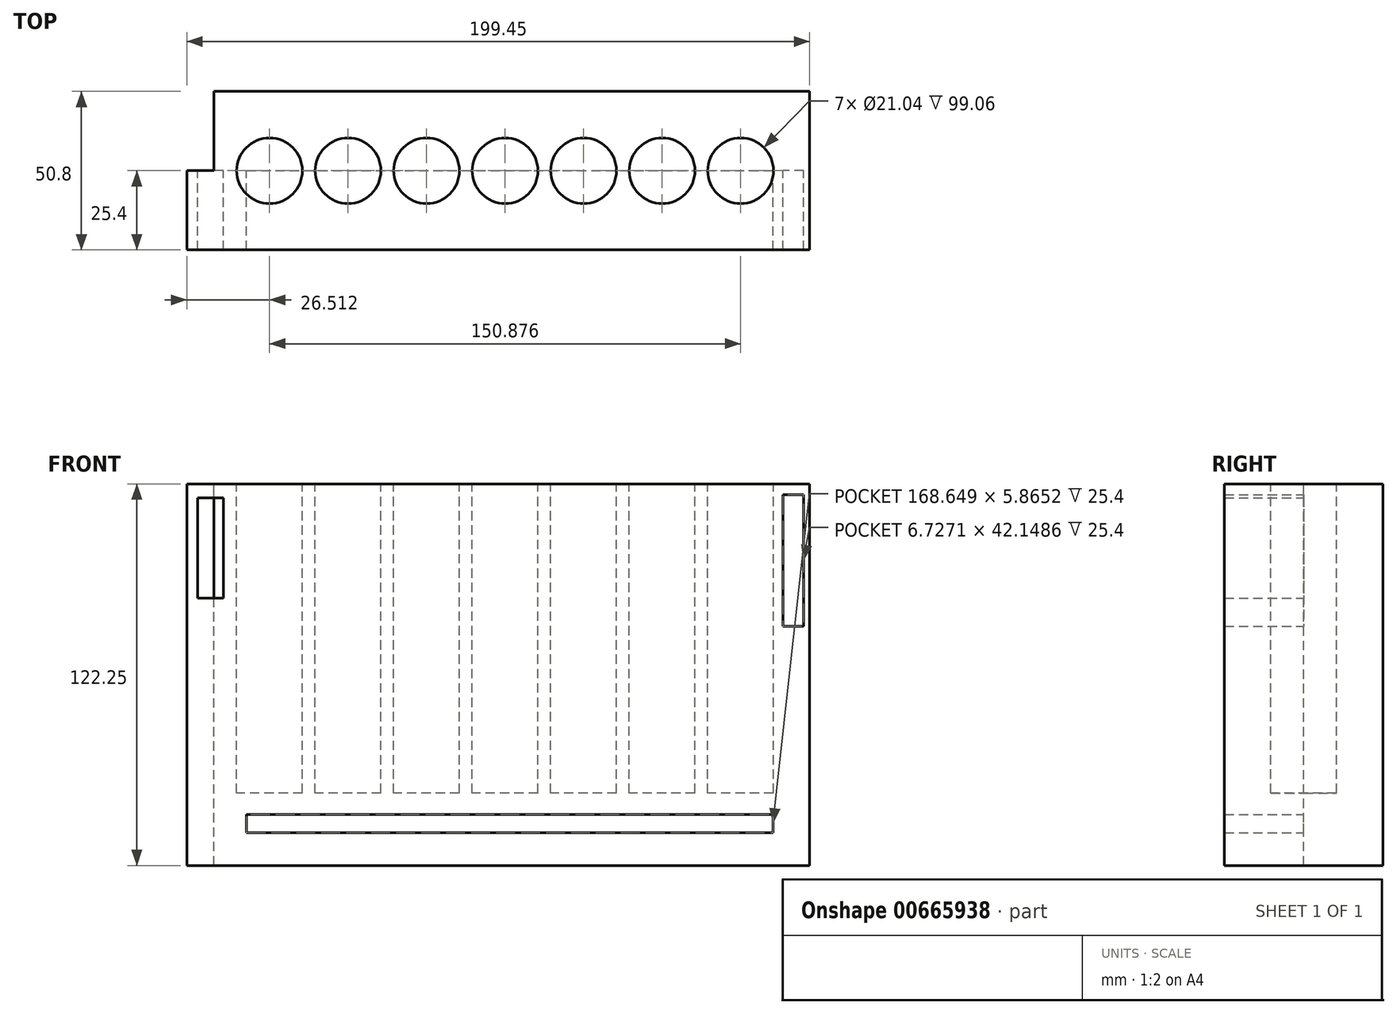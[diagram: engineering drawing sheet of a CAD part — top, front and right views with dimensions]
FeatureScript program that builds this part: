
annotation { "Feature Type Name" : "Feature", "Feature Type Description" : "" }
export const myFeature = defineFeature(function(context is Context, id is Id, definition is map)
    precondition{}
    {
        {
            var Q0;
            Q0=qCreatedBy(makeId("Front.planeOp"),FACE);
            var sketch = newSketch(context, id + "F0", { "sketchPlane" : qUnion([Q0])});
            skLineSegment(sketch, "E0.bottom", {"start": v(-91.64, -10.45) * mm, "end": v(99.17, -10.45) * mm});
            skLineSegment(sketch, "E0.top", {"start": v(-91.64, 111.8) * mm, "end": v(99.17, 111.8) * mm});
            skLineSegment(sketch, "E0.left", {"start": v(-91.64, -10.45) * mm, "end": v(-91.64, 111.8) * mm});
            skLineSegment(sketch, "E0.right", {"start": v(99.17, -10.45) * mm, "end": v(99.17, 111.8) * mm});
            skSolve(sketch);
        }
        {
            var Q0;
            Q0 = qSketchRegion(id + "F0", true);
            extrude(context, id + "F1", {"entities" : qUnion([Q0]), "depth" : 25.4 * mm, "offsetDistance" : 25.4 * mm});
        }
        {
            var Q0;
            Q0=makeQuery(id+"F1.opExtrude","SWEPT_FACE",FACE,{"disambiguationData":[OSD([sQuery(id+"F0.wireOp",EDGE,"E0.top")])]});
            var sketch = newSketch(context, id + "F2", { "sketchPlane" : qUnion([Q0])});
            skCircle(sketch, "E1", {"center": v(-73.77, -25.4) * mm, "radius": 10.52 * mm});
            skCircle(sketch, "E2.1.0.0", {"center": v(-48.62, -25.4) * mm, "radius": 10.52 * mm});
            skCircle(sketch, "E2.2.0.0", {"center": v(-23.48, -25.4) * mm, "radius": 10.52 * mm});
            skCircle(sketch, "E2.3.0.0", {"center": v(1.67, -25.4) * mm, "radius": 10.52 * mm});
            skCircle(sketch, "E2.4.0.0", {"center": v(26.82, -25.4) * mm, "radius": 10.52 * mm});
            skCircle(sketch, "E2.5.0.0", {"center": v(51.96, -25.4) * mm, "radius": 10.52 * mm});
            skCircle(sketch, "E2.6.0.0", {"center": v(77.1, -25.4) * mm, "radius": 10.52 * mm});
            skLineSegment(sketch, "E2.direction1", {"start": v(-73.77, -25.4) * mm, "end": v(-48.62, -25.4) * mm, "construction": true});
            skSolve(sketch);
        }
        {
            var Q0;
            {var subQ0=sQuery(id+"F2.wireOp",EDGE,"E1");var subQ1=makeQuery(id+"F1.opExtrude","CAP_EDGE",EDGE,{"disambiguationData":[OSD([sQuery(id+"F0.wireOp",EDGE,"E0.top")])],"isStart":false});var subQ2=makeQuery(id+"F2.imprint","INTERSECT",VERTEX,{"disambiguationData":[OD(0.0)],"derivedFrom":[subQ1,subQ0]});Q0=makeQuery(id+"F2.imprint","IMPRINT",FACE,{"disambiguationData":[TD([[makeQuery(id+"F2.imprint","IMPRINT",EDGE,{"disambiguationData":[TD([[subQ2,1.0]])],"derivedFrom":subQ0}),1.0]])]});}
            var Q1;
            {var subQ0=sQuery(id+"F2.wireOp",EDGE,"E2.1.0.0");var subQ1=makeQuery(id+"F1.opExtrude","CAP_EDGE",EDGE,{"disambiguationData":[OSD([sQuery(id+"F0.wireOp",EDGE,"E0.top")])],"isStart":false});var subQ2=makeQuery(id+"F2.imprint","INTERSECT",VERTEX,{"disambiguationData":[OD(0.0)],"derivedFrom":[subQ1,subQ0]});Q1=makeQuery(id+"F2.imprint","IMPRINT",FACE,{"disambiguationData":[TD([[makeQuery(id+"F2.imprint","IMPRINT",EDGE,{"disambiguationData":[TD([[subQ2,1.0]])],"derivedFrom":subQ0}),1.0]])]});}
            var Q2;
            {var subQ0=sQuery(id+"F2.wireOp",EDGE,"E2.2.0.0");var subQ1=makeQuery(id+"F1.opExtrude","CAP_EDGE",EDGE,{"disambiguationData":[OSD([sQuery(id+"F0.wireOp",EDGE,"E0.top")])],"isStart":false});var subQ2=makeQuery(id+"F2.imprint","INTERSECT",VERTEX,{"disambiguationData":[OD(0.0)],"derivedFrom":[subQ1,subQ0]});Q2=makeQuery(id+"F2.imprint","IMPRINT",FACE,{"disambiguationData":[TD([[makeQuery(id+"F2.imprint","IMPRINT",EDGE,{"disambiguationData":[TD([[subQ2,1.0]])],"derivedFrom":subQ0}),1.0]])]});}
            var Q3;
            {var subQ0=sQuery(id+"F2.wireOp",EDGE,"E2.3.0.0");var subQ1=makeQuery(id+"F1.opExtrude","CAP_EDGE",EDGE,{"disambiguationData":[OSD([sQuery(id+"F0.wireOp",EDGE,"E0.top")])],"isStart":false});var subQ2=makeQuery(id+"F2.imprint","INTERSECT",VERTEX,{"disambiguationData":[OD(0.0)],"derivedFrom":[subQ1,subQ0]});Q3=makeQuery(id+"F2.imprint","IMPRINT",FACE,{"disambiguationData":[TD([[makeQuery(id+"F2.imprint","IMPRINT",EDGE,{"disambiguationData":[TD([[subQ2,1.0]])],"derivedFrom":subQ0}),1.0]])]});}
            var Q4;
            {var subQ0=sQuery(id+"F2.wireOp",EDGE,"E2.4.0.0");var subQ1=makeQuery(id+"F1.opExtrude","CAP_EDGE",EDGE,{"disambiguationData":[OSD([sQuery(id+"F0.wireOp",EDGE,"E0.top")])],"isStart":false});var subQ2=makeQuery(id+"F2.imprint","INTERSECT",VERTEX,{"disambiguationData":[OD(0.0)],"derivedFrom":[subQ1,subQ0]});Q4=makeQuery(id+"F2.imprint","IMPRINT",FACE,{"disambiguationData":[TD([[makeQuery(id+"F2.imprint","IMPRINT",EDGE,{"disambiguationData":[TD([[subQ2,-1.0]])],"derivedFrom":subQ0}),1.0]])]});}
            var Q5;
            {var subQ0=sQuery(id+"F2.wireOp",EDGE,"E2.6.0.0");var subQ1=makeQuery(id+"F1.opExtrude","CAP_EDGE",EDGE,{"disambiguationData":[OSD([sQuery(id+"F0.wireOp",EDGE,"E0.top")])],"isStart":false});var subQ2=makeQuery(id+"F2.imprint","INTERSECT",VERTEX,{"disambiguationData":[OD(0.0)],"derivedFrom":[subQ1,subQ0]});Q5=makeQuery(id+"F2.imprint","IMPRINT",FACE,{"disambiguationData":[TD([[makeQuery(id+"F2.imprint","IMPRINT",EDGE,{"disambiguationData":[TD([[subQ2,-1.0]])],"derivedFrom":subQ0}),1.0]])]});}
            var Q6;
            {var subQ0=sQuery(id+"F2.wireOp",EDGE,"E2.5.0.0");var subQ1=makeQuery(id+"F1.opExtrude","CAP_EDGE",EDGE,{"disambiguationData":[OSD([sQuery(id+"F0.wireOp",EDGE,"E0.top")])],"isStart":false});var subQ2=makeQuery(id+"F2.imprint","INTERSECT",VERTEX,{"disambiguationData":[OD(0.0)],"derivedFrom":[subQ1,subQ0]});Q6=makeQuery(id+"F2.imprint","IMPRINT",FACE,{"disambiguationData":[TD([[makeQuery(id+"F2.imprint","IMPRINT",EDGE,{"disambiguationData":[TD([[subQ2,-1.0]])],"derivedFrom":subQ0}),1.0]])]});}
            extrude(context, id + "F3", {"entities" : qUnion([Q0, Q1, Q2, Q3, Q4, Q5, Q6]), "operationType" : NewBodyOperationType.REMOVE, "oppositeDirection" : true, "depth" : 99.06 * mm, "offsetDistance" : 25.4 * mm});
        }
        {
            var Q0;
            Q0=makeQuery(id+"F1.opExtrude","CAP_FACE",FACE,{"disambiguationData":[OSD([sQuery(id+"F0.wireOp",EDGE,"E0.bottom"),sQuery(id+"F0.wireOp",EDGE,"E0.top"),sQuery(id+"F0.wireOp",EDGE,"E0.left"),sQuery(id+"F0.wireOp",EDGE,"E0.right")])],"isStart":false});
            var sketch = newSketch(context, id + "F4", { "sketchPlane" : qUnion([Q0])});
            skCircle(sketch, "E3", {"center": v(-73.77, 12.74) * mm, "radius": 23.19 * mm});
            skSolve(sketch);
        }
        {
            var Q0;
            Q0=makeQuery(id+"F1.opExtrude","SWEPT_BODY",BODY,{"disambiguationData":[OSD([sQuery(id+"F0.wireOp",EDGE,"E0.bottom"),sQuery(id+"F0.wireOp",EDGE,"E0.top"),sQuery(id+"F0.wireOp",EDGE,"E0.left"),sQuery(id+"F0.wireOp",EDGE,"E0.right")])]});
            var Q1;
            {var subQ0=sQuery(id+"F0.wireOp",EDGE,"E0.right");var subQ24=makeQuery(id+"F1.opExtrude","CAP_EDGE",EDGE,{"disambiguationData":[OSD([subQ0])],"isStart":false});Q1=makeQuery(id+"F4.imprint","IMPRINT",FACE,{"disambiguationData":[TD([[makeQuery(id+"F4.imprint","IMPRINT",EDGE,{"derivedFrom":subQ24}),1.0]])]});}
            mirror(context, id + "F5", {"entities" : qUnion([Q0]), "mirrorPlane" : qUnion([Q1])});
        }
        {
            var Q0;
            Q0=makeQuery(id+"F5.opPattern","COPY",FACE,{"derivedFrom":makeQuery(id+"F1.opExtrude","CAP_FACE",FACE,{"disambiguationData":[OSD([sQuery(id+"F0.wireOp",EDGE,"E0.bottom"),sQuery(id+"F0.wireOp",EDGE,"E0.top"),sQuery(id+"F0.wireOp",EDGE,"E0.left"),sQuery(id+"F0.wireOp",EDGE,"E0.right")])],"isStart":false}),"instanceName":"1"});
            var sketch = newSketch(context, id + "F6", { "sketchPlane" : qUnion([Q0])});
            skLineSegment(sketch, "E4.bottom", {"start": v(81.13, 0) * mm, "end": v(-87.52, 0) * mm});
            skLineSegment(sketch, "E4.top", {"start": v(81.13, 5.87) * mm, "end": v(-87.52, 5.87) * mm});
            skLineSegment(sketch, "E4.left", {"start": v(81.13, 0) * mm, "end": v(81.13, 5.87) * mm});
            skLineSegment(sketch, "E4.right", {"start": v(-87.52, 0) * mm, "end": v(-87.52, 5.87) * mm});
            skSolve(sketch);
        }
        {
            var Q0;
            Q0 = qSketchRegion(id + "F6", true);
            extrude(context, id + "F7", {"entities" : qUnion([Q0]), "operationType" : NewBodyOperationType.REMOVE, "oppositeDirection" : true, "depth" : 25.4 * mm, "offsetDistance" : 25.4 * mm});
        }
        {
            var Q0;
            Q0=makeQuery(id+"F5.opPattern","COPY",FACE,{"derivedFrom":makeQuery(id+"F1.opExtrude","SWEPT_FACE",FACE,{"disambiguationData":[OSD([sQuery(id+"F0.wireOp",EDGE,"E0.left")])]}),"instanceName":"1"});
            extrude(context, id + "F8", {"entities" : qUnion([Q0]), "operationType" : NewBodyOperationType.ADD, "depth" : 8.64 * mm, "offsetDistance" : 25.4 * mm});
        }
        {
            var Q0;
            {var subQ0=sQuery(id+"F0.wireOp",EDGE,"E0.left");Q0=makeQuery(id+"F8.boolean.opBoolean","MERGE",FACE,{"derivedFrom":[makeQuery(id+"F5.opPattern","COPY",FACE,{"derivedFrom":makeQuery(id+"F1.opExtrude","CAP_FACE",FACE,{"disambiguationData":[OSD([sQuery(id+"F0.wireOp",EDGE,"E0.bottom"),sQuery(id+"F0.wireOp",EDGE,"E0.top"),subQ0,sQuery(id+"F0.wireOp",EDGE,"E0.right")])],"isStart":false}),"instanceName":"1"}),makeQuery(id+"F8.opExtrude","SWEPT_FACE",FACE,{"disambiguationData":[OSD([subQ0]),TDD([makeQuery(id+"F5.opPattern","COPY",EDGE,{"derivedFrom":makeQuery(id+"F1.opExtrude","CAP_EDGE",EDGE,{"disambiguationData":[OSD([subQ0])],"isStart":false}),"instanceName":"1"})])]})]});}
            var sketch = newSketch(context, id + "F9", { "sketchPlane" : qUnion([Q0])});
            skLineSegment(sketch, "E5.bottom", {"start": v(-97.32, 108.35) * mm, "end": v(-90.6, 108.35) * mm});
            skLineSegment(sketch, "E5.top", {"start": v(-97.32, 66.2) * mm, "end": v(-90.6, 66.2) * mm});
            skLineSegment(sketch, "E5.left", {"start": v(-97.32, 108.35) * mm, "end": v(-97.32, 66.2) * mm});
            skLineSegment(sketch, "E5.right", {"start": v(-90.6, 108.35) * mm, "end": v(-90.6, 66.2) * mm});
            skLineSegment(sketch, "E6.bottom", {"start": v(88.53, 107.38) * mm, "end": v(96.8, 107.38) * mm});
            skLineSegment(sketch, "E6.top", {"start": v(88.53, 75.25) * mm, "end": v(96.8, 75.25) * mm});
            skLineSegment(sketch, "E6.left", {"start": v(88.53, 107.38) * mm, "end": v(88.53, 75.25) * mm});
            skLineSegment(sketch, "E6.right", {"start": v(96.8, 107.38) * mm, "end": v(96.8, 75.25) * mm});
            skSolve(sketch);
        }
        {
            var Q0;
            Q0 = qSketchRegion(id + "F9", true);
            extrude(context, id + "F10", {"entities" : qUnion([Q0]), "operationType" : NewBodyOperationType.REMOVE, "oppositeDirection" : true, "depth" : 25.4 * mm, "offsetDistance" : 25.4 * mm});
        }
    });
